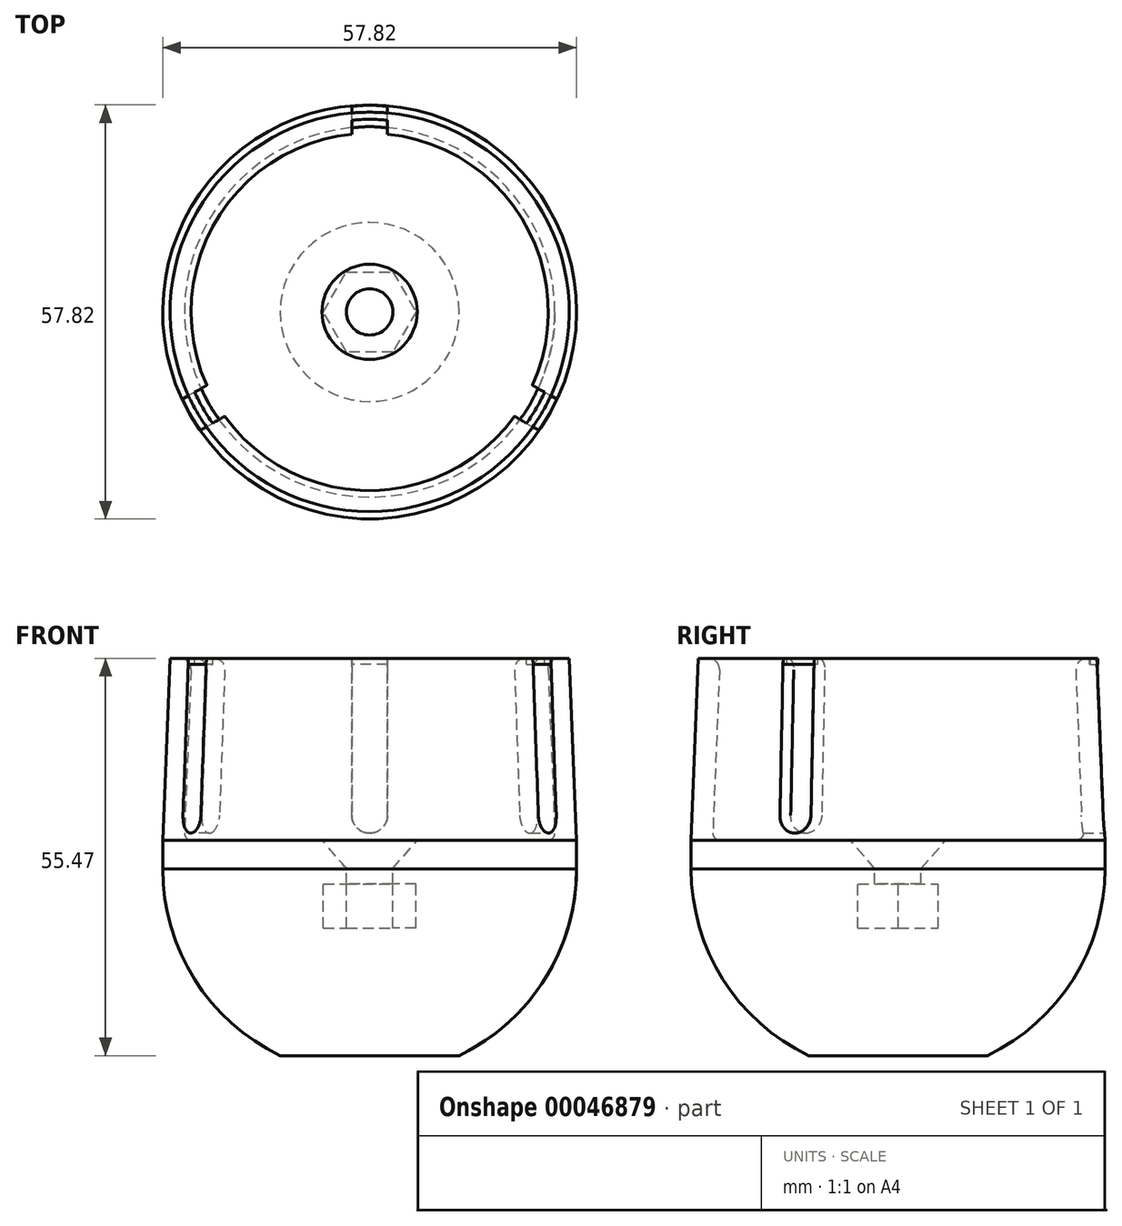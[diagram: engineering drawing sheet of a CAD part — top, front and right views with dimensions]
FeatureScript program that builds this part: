
annotation { "Feature Type Name" : "Feature", "Feature Type Description" : "" }
export const myFeature = defineFeature(function(context is Context, id is Id, definition is map)
    precondition{}
    {
        {
            var Q0;
            Q0=qCreatedBy(makeId("Front.planeOp"),FACE);
            var sketch = newSketch(context, id + "F0", { "sketchPlane" : qUnion([Q0])});
            skLineSegment(sketch, "E0", {"start": v(0, 0) * mm, "end": v(-25.9, 0) * mm});
            skLineSegment(sketch, "E1", {"start": v(-25.9, 0) * mm, "end": v(-24.9, 25.4) * mm});
            skLineSegment(sketch, "E2", {"start": v(-24.9, 25.4) * mm, "end": v(-27.9, 25.4) * mm});
            skLineSegment(sketch, "E3", {"start": v(-27.9, 25.4) * mm, "end": v(-28.9, 0) * mm});
            skLineSegment(sketch, "E4", {"start": v(0, 0) * mm, "end": v(0, -4) * mm});
            skLineSegment(sketch, "E5", {"start": v(0, -4) * mm, "end": v(-28.9, -4) * mm});
            skLineSegment(sketch, "E6", {"start": v(-28.9, -4) * mm, "end": v(-28.9, 0) * mm});
            skSolve(sketch);
        }
        {
            var Q0;
            Q0 = qSketchRegion(id + "F0", true);
            var Q1;
            Q1=sQuery(id+"F0.wireOp",EDGE,"E4");
            revolve(context, id + "F1", {"entities" : qUnion([Q0]), "axis" : qUnion([Q1]), "revolveType" : RevolveType.FULL});
        }
        {
            var Q0;
            Q0=makeQuery(id+"F1.opRevolve","SWEPT_EDGE",EDGE,{"disambiguationData":[OSD([sQuery(id+"F0.wireOp",EDGE,"E0"),sQuery(id+"F0.wireOp",EDGE,"E1")])]});
            fillet(context, id + "F2", {"entities" : qUnion([Q0]), "radius" : 1 * mm, "allowEdgeOverflow" : false});
        }
        {
            var Q0;
            Q0=makeQuery(id+"F1.opRevolve","SWEPT_EDGE",EDGE,{"disambiguationData":[OSD([sQuery(id+"F0.wireOp",EDGE,"E1"),sQuery(id+"F0.wireOp",EDGE,"E2")])]});
            fillet(context, id + "F3", {"entities" : qUnion([Q0]), "radius" : 1.5 * mm, "allowEdgeOverflow" : false});
        }
        {
            var Q0;
            Q0=makeQuery(id+"F1.opRevolve","SWEPT_FACE",FACE,{"disambiguationData":[OSD([sQuery(id+"F0.wireOp",EDGE,"E2")])]});
            var sketch = newSketch(context, id + "F4", { "sketchPlane" : qUnion([Q0])});
            skLineSegment(sketch, "E7.bottom", {"start": v(-2.5, 32.82) * mm, "end": v(2.5, 32.82) * mm});
            skLineSegment(sketch, "E7.top", {"start": v(-2.5, 0) * mm, "end": v(2.5, 0) * mm});
            skLineSegment(sketch, "E7.left", {"start": v(-2.5, 32.82) * mm, "end": v(-2.5, 0) * mm});
            skLineSegment(sketch, "E7.right", {"start": v(2.5, 32.82) * mm, "end": v(2.5, 0) * mm});
            skLineSegment(sketch, "E8.1.0", {"start": v(-29.67, -14.25) * mm, "end": v(-1.25, 2.17) * mm});
            skLineSegment(sketch, "E8.1.1", {"start": v(-27.17, -18.58) * mm, "end": v(1.25, -2.17) * mm});
            skLineSegment(sketch, "E8.1.2", {"start": v(1.25, -2.17) * mm, "end": v(-1.25, 2.17) * mm});
            skLineSegment(sketch, "E8.1.3", {"start": v(-27.17, -18.58) * mm, "end": v(-29.67, -14.25) * mm});
            skLineSegment(sketch, "E8.2.0", {"start": v(27.17, -18.58) * mm, "end": v(-1.25, -2.17) * mm});
            skLineSegment(sketch, "E8.2.1", {"start": v(29.67, -14.25) * mm, "end": v(1.25, 2.17) * mm});
            skLineSegment(sketch, "E8.2.2", {"start": v(1.25, 2.17) * mm, "end": v(-1.25, -2.17) * mm});
            skLineSegment(sketch, "E8.2.3", {"start": v(29.67, -14.25) * mm, "end": v(27.17, -18.58) * mm});
            skPoint(sketch, "E8.center", {"position": v(0, 0) * mm});
            skSolve(sketch);
        }
        {
            var Q0;
            Q0 = qSketchRegion(id + "F4", true);
            var Q1;
            Q1=makeQuery(id+"F2.opFillet","BLEND_FACE",FACE,{"disambiguationData":[OSD([sQuery(id+"F0.wireOp",EDGE,"E0"),sQuery(id+"F0.wireOp",EDGE,"E1")])]});
            extrude(context, id + "F5", {"entities" : qUnion([Q0]), "operationType" : NewBodyOperationType.REMOVE, "oppositeDirection" : true, "endBoundEntityFace" : qUnion([Q1]), "depth" : (25.4 - 1) * mm});
        }
        {
            var Q0;
            Q0=makeQuery(id+"F5.boolean.opBoolean","COPY",EDGE,{"derivedFrom":makeQuery(id+"F5.opExtrude","CAP_EDGE",EDGE,{"disambiguationData":[OSD([sQuery(id+"F4.wireOp",EDGE,"E8.1.0")])],"isStart":false})});
            var Q1;
            Q1=makeQuery(id+"F5.boolean.opBoolean","COPY",EDGE,{"derivedFrom":makeQuery(id+"F5.opExtrude","CAP_EDGE",EDGE,{"disambiguationData":[OSD([sQuery(id+"F4.wireOp",EDGE,"E8.1.1")])],"isStart":false})});
            var Q2;
            Q2=makeQuery(id+"F5.boolean.opBoolean","COPY",EDGE,{"derivedFrom":makeQuery(id+"F5.opExtrude","CAP_EDGE",EDGE,{"disambiguationData":[OSD([sQuery(id+"F4.wireOp",EDGE,"E8.2.0")])],"isStart":false})});
            var Q3;
            Q3=makeQuery(id+"F5.boolean.opBoolean","COPY",EDGE,{"derivedFrom":makeQuery(id+"F5.opExtrude","CAP_EDGE",EDGE,{"disambiguationData":[OSD([sQuery(id+"F4.wireOp",EDGE,"E8.2.1")])],"isStart":false})});
            var Q4;
            Q4=makeQuery(id+"F5.boolean.opBoolean","COPY",EDGE,{"derivedFrom":makeQuery(id+"F5.opExtrude","CAP_EDGE",EDGE,{"disambiguationData":[OSD([sQuery(id+"F4.wireOp",EDGE,"E7.right")])],"isStart":false})});
            var Q5;
            Q5=makeQuery(id+"F5.boolean.opBoolean","COPY",EDGE,{"derivedFrom":makeQuery(id+"F5.opExtrude","CAP_EDGE",EDGE,{"disambiguationData":[OSD([sQuery(id+"F4.wireOp",EDGE,"E7.left")])],"isStart":false})});
            fillet(context, id + "F6", {"entities" : qUnion([Q0, Q1, Q2, Q3, Q4, Q5]), "radius" : 2.5 * mm, "allowEdgeOverflow" : false});
        }
        {
            var Q0;
            {var subQ0=sQuery(id+"F0.wireOp",EDGE,"E2");Q0=makeQuery(id+"F5.boolean.opBoolean","SPLIT",FACE,{"disambiguationData":[TD([makeQuery(id+"F5.opExtrude","SWEPT_FACE",FACE,{"disambiguationData":[OSD([sQuery(id+"F4.wireOp",EDGE,"E7.left")])]})])],"derivedFrom":makeQuery(id+"F1.opRevolve","SWEPT_FACE",FACE,{"disambiguationData":[OSD([subQ0])]})});}
            var sketch = newSketch(context, id + "F7", { "sketchPlane" : qUnion([Q0])});
            skArc(sketch, "E9.0", {"start": v(-2.5, 27.78) * mm, "mid": v(-24.16, 13.95) * mm, "end": v(-25.3, -11.72) * mm, "construction": true});
            skCircle(sketch, "E10", {"center": v(0, 0) * mm, "radius": 27.9 * mm});
            skCircle(sketch, "E11", {"center": v(0, 0) * mm, "radius": 26.9 * mm});
            skLineSegment(sketch, "E12", {"start": v(0, 0) * mm, "end": v(0, 27.9) * mm, "construction": true});
            skPoint(sketch, "E13", {"position": v(0, 26.9) * mm});
            skSolve(sketch);
        }
        {
            var Q0;
            Q0=qCreatedBy(makeId("Front.planeOp"),FACE);
            var sketch = newSketch(context, id + "F8", { "sketchPlane" : qUnion([Q0])});
            skLineSegment(sketch, "E14", {"start": v(0, 11.3) * mm, "end": v(0, -15.68) * mm});
            skLineSegment(sketch, "E15", {"start": v(0, -15.68) * mm, "end": v(-3.17, -15.68) * mm});
            skLineSegment(sketch, "E16", {"start": v(-3.17, -15.68) * mm, "end": v(-3.17, -4) * mm, "construction": true});
            skLineSegment(sketch, "E17", {"start": v(-3.17, -4) * mm, "end": v(-6.65, -4) * mm, "construction": true});
            skLineSegment(sketch, "E18", {"start": v(-6.65, 11.3) * mm, "end": v(0, 11.3) * mm});
            skLineSegment(sketch, "E19", {"start": v(-3.17, -4) * mm, "end": v(-6.65, 0) * mm});
            skLineSegment(sketch, "E20", {"start": v(-6.65, 0) * mm, "end": v(0, 0) * mm});
            skLineSegment(sketch, "E21", {"start": v(-6.65, 11.3) * mm, "end": v(-6.65, 0) * mm});
            skLineSegment(sketch, "E22", {"start": v(-6.65, -4) * mm, "end": v(-6.65, 0) * mm, "construction": true});
            skLineSegment(sketch, "E23", {"start": v(-3.24, -15.68) * mm, "end": v(-3.24, -3.93) * mm});
            skLineSegment(sketch, "E24", {"start": v(0, -15.68) * mm, "end": v(-3.24, -15.68) * mm});
            skSolve(sketch);
        }
        {
            var Q0;
            Q0 = qSketchRegion(id + "F8", true);
            var Q1;
            Q1=sQuery(id+"F8.wireOp",EDGE,"E14");
            revolve(context, id + "F9", {"operationType" : NewBodyOperationType.REMOVE, "entities" : qUnion([Q0]), "axis" : qUnion([Q1]), "revolveType" : RevolveType.FULL, "oppositeDirection" : true});
        }
        {
            var Q0;
            Q0=qCreatedBy(makeId("Front.planeOp"),FACE);
            var sketch = newSketch(context, id + "F10", { "sketchPlane" : qUnion([Q0])});
            skLineSegment(sketch, "E25.0", {"start": v(-28.9, -4) * mm, "end": v(0, -4) * mm});
            skLineSegment(sketch, "E26", {"start": v(0, -4) * mm, "end": v(28.9, -4) * mm, "construction": true});
            skLineSegment(sketch, "E27", {"start": v(0, -4) * mm, "end": v(0, -30.07) * mm});
            skArc(sketch, "E28", {"start": v(-28.9, -4) * mm, "mid": v(-24.46, -19.4) * mm, "end": v(-12.5, -30.07) * mm});
            skLineSegment(sketch, "E29", {"start": v(0, -30.07) * mm, "end": v(-12.5, -30.07) * mm});
            skArc(sketch, "E30", {"start": v(-12.5, -30.07) * mm, "mid": v(-6.4, -32.19) * mm, "end": v(0, -32.9) * mm, "construction": true});
            skLineSegment(sketch, "E31", {"start": v(0, -30.07) * mm, "end": v(0, -32.9) * mm, "construction": true});
            skSolve(sketch);
        }
        {
            var Q0;
            Q0 = qSketchRegion(id + "F10", true);
            var Q1;
            Q1=sQuery(id+"F10.wireOp",EDGE,"E27");
            revolve(context, id + "F11", {"entities" : qUnion([Q0]), "axis" : qUnion([Q1]), "revolveType" : RevolveType.FULL});
        }
        {
            var Q0;
            Q0=makeQuery(id+"F11.opRevolve","SWEPT_FACE",FACE,{"disambiguationData":[OSD([sQuery(id+"F10.wireOp",EDGE,"E25.0")])]});
            var sketch = newSketch(context, id + "F12", { "sketchPlane" : qUnion([Q0])});
            skCircle(sketch, "E32.cCircle", {"center": v(0, 0) * mm, "radius": 5.6 * mm, "construction": true});
            skLineSegment(sketch, "E32.0", {"start": v(-3.23, 5.6) * mm, "end": v(3.23, 5.6) * mm});
            skLineSegment(sketch, "E32.1", {"start": v(3.23, 5.6) * mm, "end": v(6.47, 0) * mm});
            skLineSegment(sketch, "E32.2", {"start": v(6.47, 0) * mm, "end": v(3.23, -5.6) * mm});
            skLineSegment(sketch, "E32.3", {"start": v(3.23, -5.6) * mm, "end": v(-3.23, -5.6) * mm});
            skLineSegment(sketch, "E32.4", {"start": v(-3.23, -5.6) * mm, "end": v(-6.47, 0) * mm});
            skLineSegment(sketch, "E32.5", {"start": v(-6.47, 0) * mm, "end": v(-3.23, 5.6) * mm});
            skPoint(sketch, "E32.0.midPoint", {"position": v(0, 5.6) * mm});
            skSolve(sketch);
        }
        {
            var Q0;
            Q0 = qSketchRegion(id + "F12", true);
            extrude(context, id + "F13", {"entities" : qUnion([Q0]), "oppositeDirection" : true, "depth" : 6.2 * mm});
        }
        {
            var Q0;
            Q0=makeQuery(id+"F13.opExtrude","SWEPT_BODY",BODY,{"disambiguationData":[OSD([sQuery(id+"F12.wireOp",EDGE,"E32.0"),sQuery(id+"F12.wireOp",EDGE,"E32.1"),sQuery(id+"F12.wireOp",EDGE,"E32.2"),sQuery(id+"F12.wireOp",EDGE,"E32.3"),sQuery(id+"F12.wireOp",EDGE,"E32.4"),sQuery(id+"F12.wireOp",EDGE,"E32.5")])]});
            var Q1;
            Q1=makeQuery(id+"F11.opRevolve","SWEPT_FACE",FACE,{"disambiguationData":[OSD([sQuery(id+"F10.wireOp",EDGE,"E25.0")])]});
            transform(context, id + "F14", {"entities" : qUnion([Q0]), "transformType" : TransformType.TRANSLATION_DISTANCE, "transformDirection" : qUnion([Q1]), "distance" : 2.06 * mm, "oppositeDirection" : true, "makeCopy" : false});
        }
        {
            var Q0;
            Q0=makeQuery(id+"F13.opExtrude","SWEPT_BODY",BODY,{"disambiguationData":[OSD([sQuery(id+"F12.wireOp",EDGE,"E32.0"),sQuery(id+"F12.wireOp",EDGE,"E32.1"),sQuery(id+"F12.wireOp",EDGE,"E32.2"),sQuery(id+"F12.wireOp",EDGE,"E32.3"),sQuery(id+"F12.wireOp",EDGE,"E32.4"),sQuery(id+"F12.wireOp",EDGE,"E32.5")])]});
            var Q1;
            Q1=makeQuery(id+"F11.opRevolve","SWEPT_BODY",BODY,{"disambiguationData":[OSD([sQuery(id+"F10.wireOp",EDGE,"E25.0"),sQuery(id+"F10.wireOp",EDGE,"E27"),sQuery(id+"F10.wireOp",EDGE,"E28"),sQuery(id+"F10.wireOp",EDGE,"E29")])]});
            booleanBodies(context, id + "F15", {"operationType" : BooleanOperationType.SUBTRACTION, "tools" : qUnion([Q0]), "targets" : qUnion([Q1])});
        }
        {
            var Q0;
            Q0=makeQuery(id+"F11.opRevolve","SWEPT_FACE",FACE,{"disambiguationData":[OSD([sQuery(id+"F10.wireOp",EDGE,"E25.0")])]});
            var sketch = newSketch(context, id + "F16", { "sketchPlane" : qUnion([Q0])});
            skCircle(sketch, "E33.0", {"center": v(0, 0) * mm, "radius": 3.24 * mm});
            skSolve(sketch);
        }
        {
            var Q0;
            Q0 = qSketchRegion(id + "F16", true);
            extrude(context, id + "F17", {"entities" : qUnion([Q0]), "operationType" : NewBodyOperationType.REMOVE, "oppositeDirection" : true, "depth" : 2.06 * mm});
        }
        {
            var Q0;
            Q0 = qSketchRegion(id + "F7", true);
            extrude(context, id + "F18", {"entities" : qUnion([Q0]), "operationType" : NewBodyOperationType.ADD, "oppositeDirection" : true, "depth" : 0.8 * mm});
        }
    });
